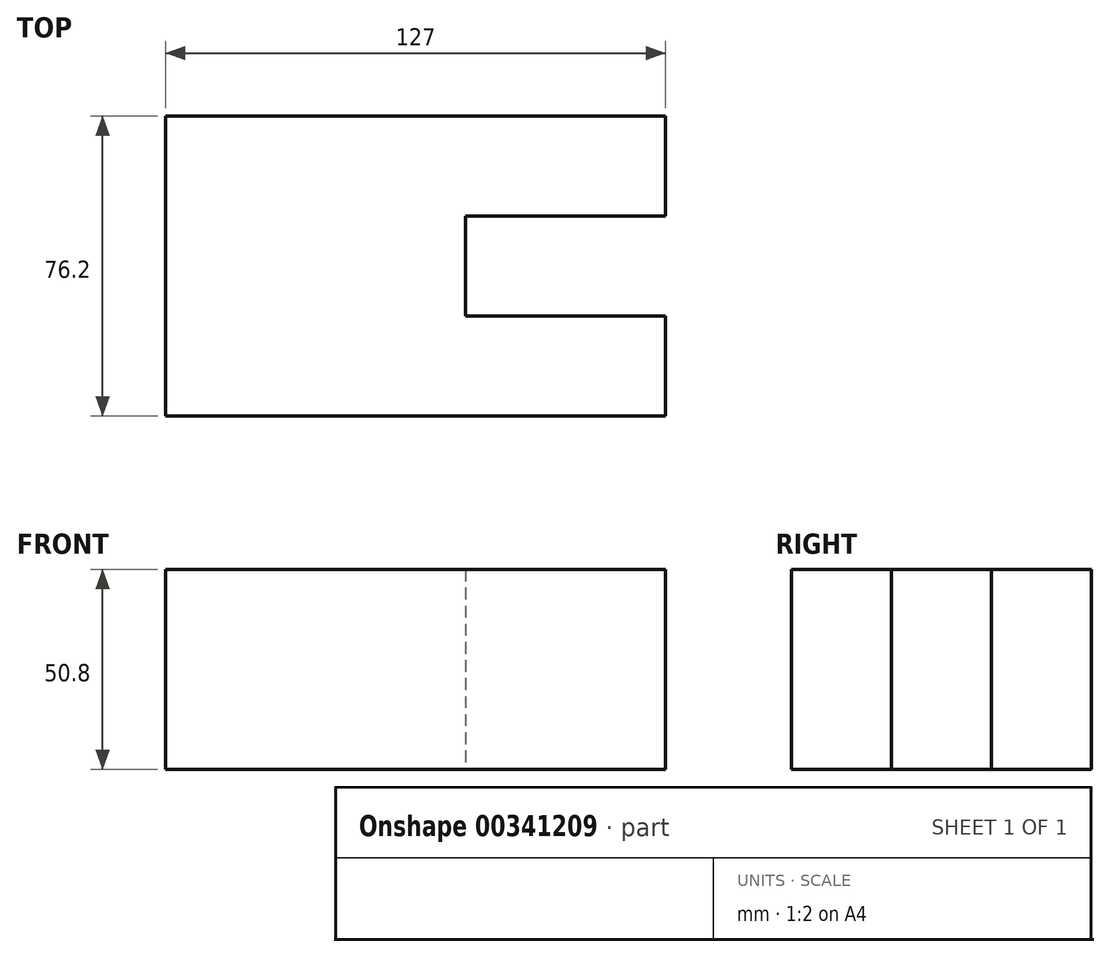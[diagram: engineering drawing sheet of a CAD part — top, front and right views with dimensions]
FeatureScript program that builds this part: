
annotation { "Feature Type Name" : "Feature", "Feature Type Description" : "" }
export const myFeature = defineFeature(function(context is Context, id is Id, definition is map)
    precondition{}
    {
        {
            var Q0;
            Q0=qCreatedBy(makeId("Top.planeOp"),FACE);
            var sketch = newSketch(context, id + "F0", { "sketchPlane" : qUnion([Q0])});
            skLineSegment(sketch, "E0", {"start": v(0, 0) * mm, "end": v(0, 76.2) * mm});
            skLineSegment(sketch, "E1", {"start": v(0, 76.2) * mm, "end": v(127, 76.2) * mm});
            skLineSegment(sketch, "E2", {"start": v(127, 76.2) * mm, "end": v(127, 50.8) * mm});
            skLineSegment(sketch, "E3", {"start": v(127, 50.8) * mm, "end": v(76.2, 50.8) * mm});
            skLineSegment(sketch, "E4", {"start": v(76.2, 50.8) * mm, "end": v(76.2, 25.4) * mm});
            skLineSegment(sketch, "E5", {"start": v(76.2, 25.4) * mm, "end": v(127, 25.4) * mm});
            skLineSegment(sketch, "E6", {"start": v(127, 25.4) * mm, "end": v(127, 0) * mm});
            skLineSegment(sketch, "E7", {"start": v(127, 0) * mm, "end": v(0, 0) * mm});
            skSolve(sketch);
        }
        {
            var Q0;
            Q0 = qSketchRegion(id + "F0", true);
            extrude(context, id + "F1", {"entities" : qUnion([Q0]), "depth" : 50.8 * mm});
        }
    });
